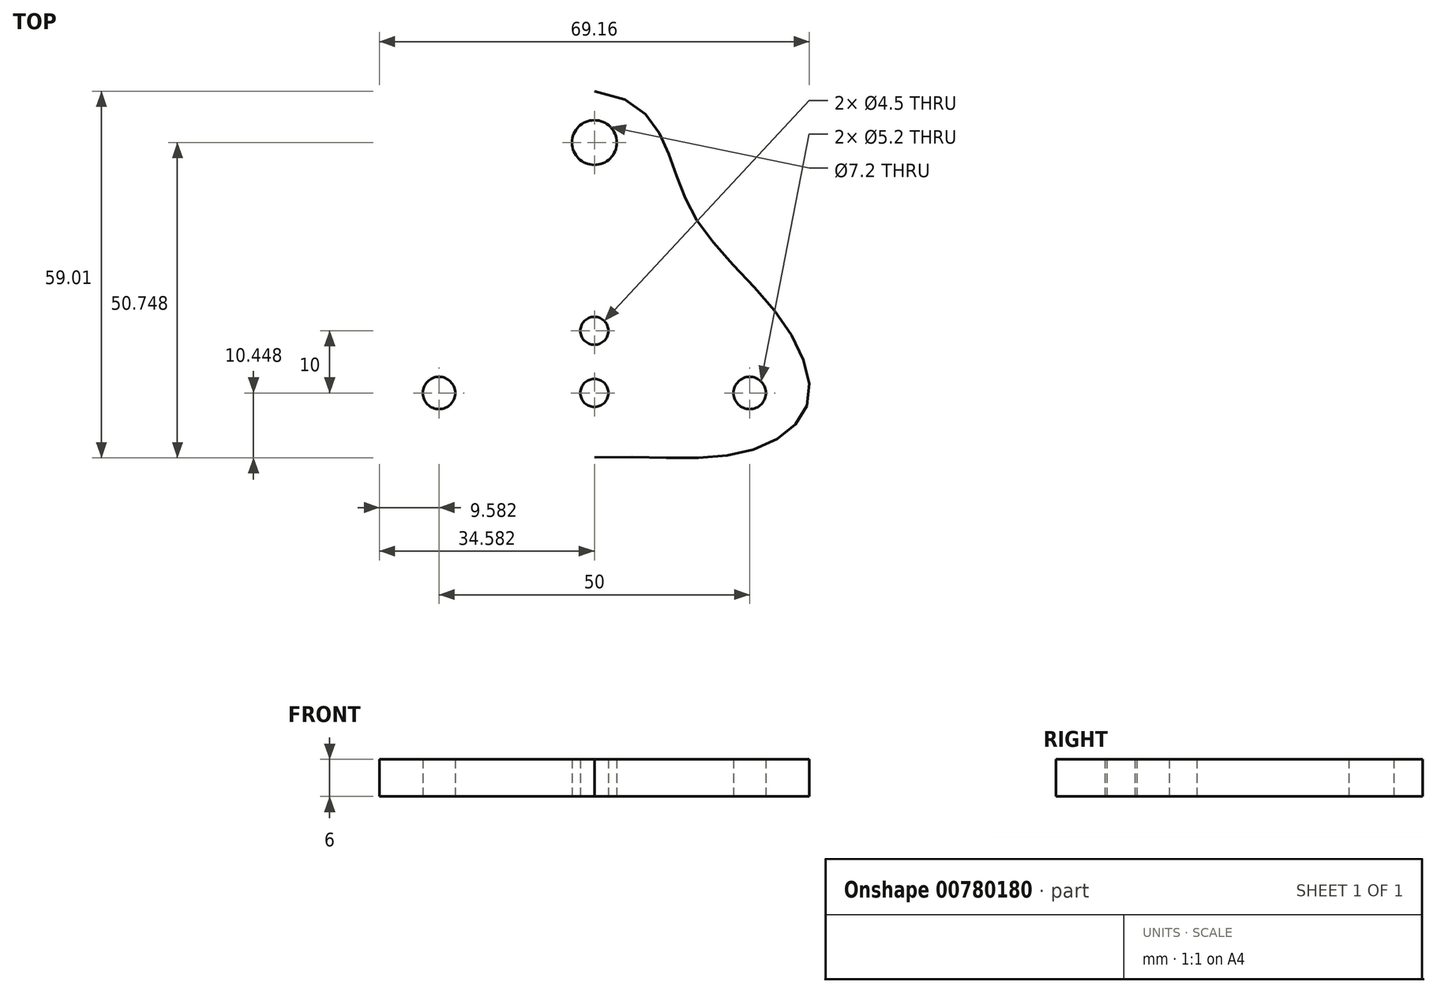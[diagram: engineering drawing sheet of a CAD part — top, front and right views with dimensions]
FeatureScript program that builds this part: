
annotation { "Feature Type Name" : "Feature", "Feature Type Description" : "" }
export const myFeature = defineFeature(function(context is Context, id is Id, definition is map)
    precondition{}
    {
        {
            var Q0;
            Q0=qCreatedBy(makeId("Top.planeOp"),FACE);
            var sketch = newSketch(context, id + "F0", { "sketchPlane" : qUnion([Q0])});
            skCircle(sketch, "E0", {"center": v(12.38, 2.73) * mm, "radius": 3.6 * mm});
            skCircle(sketch, "E1", {"center": v(37.38, -37.57) * mm, "radius": 2.6 * mm});
            skCircle(sketch, "E2", {"center": v(-12.62, -37.57) * mm, "radius": 2.6 * mm});
            skLineSegment(sketch, "E3", {"start": v(12.38, 2.25) * mm, "end": v(12.38, -52.9) * mm, "construction": true});
            skFitSpline(sketch, "E4", {"points": [v(12.38, 11) * mm, v(23.76, 2.25) * mm, v(29, -10) * mm, v(42.5, -25.85) * mm, v(46.57, -39.52) * mm, v(36.68, -47.08) * mm, v(12.38, -47.96) * mm], "startDerivative": vector(133.94, -15.63) * mm, "endDerivative": vector(-145.53, -5.3) * mm});
            skFitSpline(sketch, "E5.MirrorCS", {"points": [v(12.38, 11) * mm, v(1, 2.25) * mm, v(-4.24, -10) * mm, v(-17.74, -25.85) * mm, v(-21.8, -39.52) * mm, v(-11.91, -47.08) * mm, v(12.38, -47.96) * mm], "startDerivative": vector(-133.94, -15.63) * mm, "endDerivative": vector(145.53, -5.3) * mm});
            skCircle(sketch, "E6", {"center": v(12.38, -37.57) * mm, "radius": 2.25 * mm});
            skCircle(sketch, "E7", {"center": v(12.38, -27.57) * mm, "radius": 2.25 * mm});
            skSolve(sketch);
        }
        {
            var Q0;
            Q0=qSketchRegion(id+"F0",true);
            extrude(context, id + "F1", {"entities" : qUnion([Q0]), "depth" : 6 * mm, "offsetDistance" : 25 * mm});
        }
        {
            var Q0;
            Q0=makeQuery(id+"F1.opExtrude","CAP_FACE",FACE,{"disambiguationData":[OSD([sQuery(id+"F0.wireOp",EDGE,"E0"),sQuery(id+"F0.wireOp",EDGE,"E1"),sQuery(id+"F0.wireOp",EDGE,"E2"),sQuery(id+"F0.wireOp",EDGE,"dVXcSlPP-XXvO-6OeD-0uax-jvAfKnYlGIrO"),sQuery(id+"F0.wireOp",EDGE,"gXV22Ezd-BxGV-p7MN-5mEq-ep9CFymhMpRn"),sQuery(id+"F0.wireOp",EDGE,"WmkqfEUB-IWB8-ESqq-jCjN-kpA6IxgFtCK6"),sQuery(id+"F0.wireOp",EDGE,"E4"),sQuery(id+"F0.wireOp",EDGE,"E5.MirrorCS")])],"isStart":false});
            var sketch = newSketch(context, id + "F2", { "sketchPlane" : qUnion([Q0])});
            skCircle(sketch, "E8", {"center": v(13.2, -12.8) * mm, "radius": 8.8 * mm});
            skCircle(sketch, "E9", {"center": v(2.84, -28.45) * mm, "radius": 6.03 * mm});
            skCircle(sketch, "E10", {"center": v(22.14, -29.31) * mm, "radius": 6.13 * mm});
            skSolve(sketch);
        }
    });
